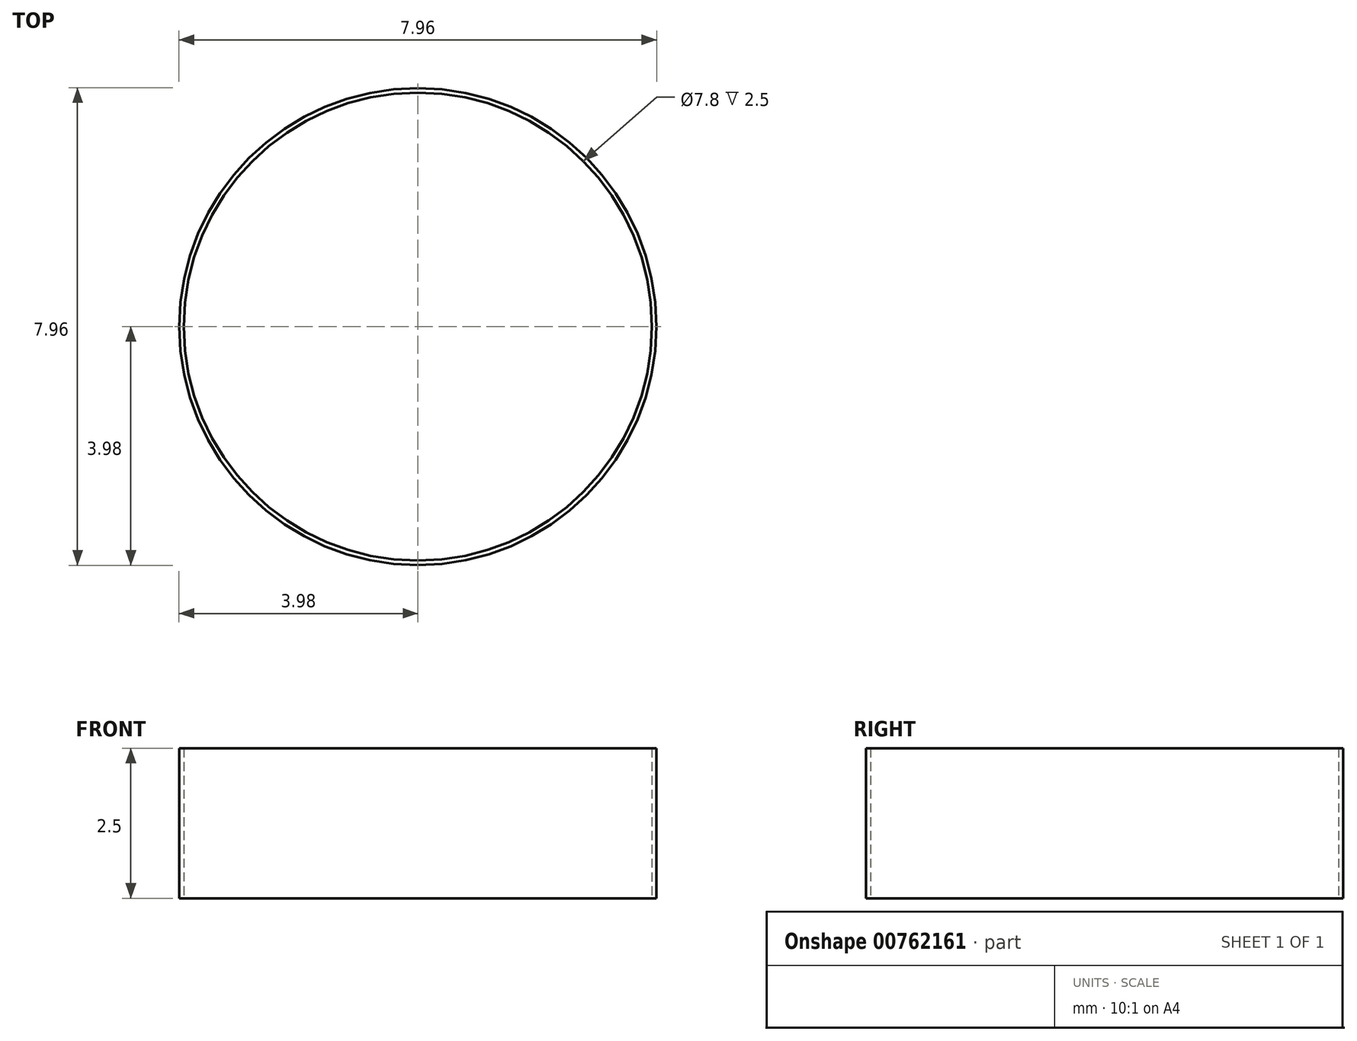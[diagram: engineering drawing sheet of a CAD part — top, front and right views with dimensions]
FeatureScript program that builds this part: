
annotation { "Feature Type Name" : "Feature", "Feature Type Description" : "" }
export const myFeature = defineFeature(function(context is Context, id is Id, definition is map)
    precondition{}
    {
        {
            var Q0;
            Q0=qCreatedBy(makeId("Top.planeOp"),FACE);
            var sketch = newSketch(context, id + "F0", { "sketchPlane" : qUnion([Q0])});
            skCircle(sketch, "E0", {"center": v(0, 0) * mm, "radius": 3.9 * mm});
            skCircle(sketch, "E1", {"center": v(0, 0) * mm, "radius": 3.98 * mm});
            skSolve(sketch);
        }
        {
            var Q0;
            Q0 = qSketchRegion(id + "F0", true);
            extrude(context, id + "F1", {"entities" : qUnion([Q0]), "depth" : 2.5 * mm, "offsetDistance" : 25.4 * mm});
        }
    });
